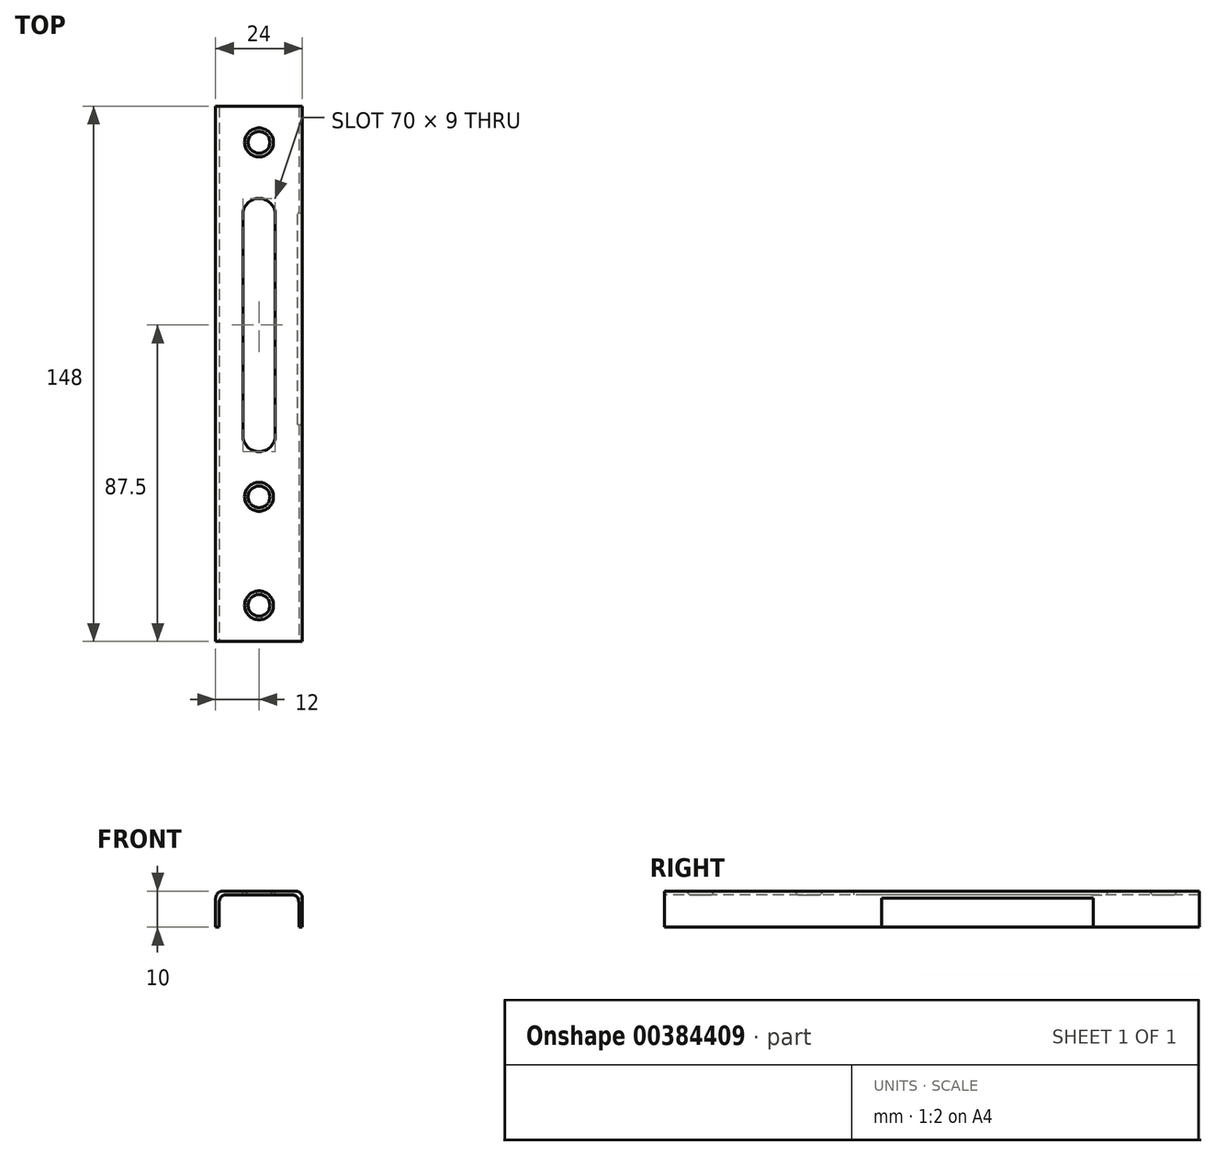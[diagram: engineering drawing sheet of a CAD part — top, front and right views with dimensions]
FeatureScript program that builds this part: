
annotation { "Feature Type Name" : "Feature", "Feature Type Description" : "" }
export const myFeature = defineFeature(function(context is Context, id is Id, definition is map)
    precondition{}
    {
        {
            var Q0;
            Q0=qCreatedBy(makeId("Top.planeOp"),FACE);
            var sketch = newSketch(context, id + "F0", { "sketchPlane" : qUnion([Q0])});
            skLineSegment(sketch, "E0", {"start": v(0, 0) * mm, "end": v(0, 148) * mm});
            skLineSegment(sketch, "E1", {"start": v(0, 148) * mm, "end": v(24, 148) * mm});
            skLineSegment(sketch, "E2", {"start": v(24, 148) * mm, "end": v(24, 0) * mm});
            skLineSegment(sketch, "E3", {"start": v(24, 0) * mm, "end": v(0, 0) * mm});
            skSolve(sketch);
        }
        {
            var Q0;
            Q0 = qSketchRegion(id + "F0", true);
            extrude(context, id + "F1", {"entities" : qUnion([Q0]), "depth" : 10 * mm});
        }
        {
            var Q0;
            Q0=makeQuery(id+"F1.opExtrude","CAP_EDGE",EDGE,{"disambiguationData":[OSD([sQuery(id+"F0.wireOp",EDGE,"E0")])],"isStart":false});
            fillet(context, id + "F2", {"entities" : qUnion([Q0]), "radius" : 2 * mm, "tangentPropagation" : true, "allowEdgeOverflow" : false});
        }
        {
            var Q0;
            Q0=makeQuery(id+"F1.opExtrude","SWEPT_FACE",FACE,{"disambiguationData":[OSD([sQuery(id+"F0.wireOp",EDGE,"E3")])]});
            var sketch = newSketch(context, id + "F3", { "sketchPlane" : qUnion([Q0])});
            skLineSegment(sketch, "E4", {"start": v(1, 0) * mm, "end": v(1, 9) * mm});
            skLineSegment(sketch, "E5", {"start": v(1, 9) * mm, "end": v(23, 9) * mm});
            skLineSegment(sketch, "E6", {"start": v(23, 9) * mm, "end": v(23, 0) * mm});
            skSolve(sketch);
        }
        {
            var Q0;
            Q0 = qSketchRegion(id + "F3", true);
            var Q1;
            {var subQ0=sQuery(id+"F3.wireOp",EDGE,"E4");Q1=makeQuery(id+"F3.imprint","IMPRINT",FACE,{"disambiguationData":[TD([[makeQuery(id+"F3.imprint","IMPRINT",EDGE,{"derivedFrom":subQ0}),-1.0]])]});}
            extrude(context, id + "F4", {"entities" : qUnion([Q0, Q1]), "operationType" : NewBodyOperationType.REMOVE, "endBound" : BoundingType.UP_TO_NEXT, "oppositeDirection" : true, "depth" : 25 * mm});
        }
        {
            var Q0;
            Q0=makeQuery(id+"F4.boolean.opBoolean","COPY",EDGE,{"derivedFrom":makeQuery(id+"F4.opExtrude","SWEPT_EDGE",EDGE,{"disambiguationData":[OSD([sQuery(id+"F3.wireOp",EDGE,"E4"),sQuery(id+"F3.wireOp",EDGE,"E5")])]})});
            fillet(context, id + "F5", {"entities" : qUnion([Q0]), "radius" : 2 * mm, "tangentPropagation" : true, "allowEdgeOverflow" : false});
        }
        {
            var Q0;
            Q0=makeQuery(id+"F1.opExtrude","CAP_FACE",FACE,{"disambiguationData":[OSD([sQuery(id+"F0.wireOp",EDGE,"E0"),sQuery(id+"F0.wireOp",EDGE,"E1"),sQuery(id+"F0.wireOp",EDGE,"E2"),sQuery(id+"F0.wireOp",EDGE,"E3")])],"isStart":false});
            var sketch = newSketch(context, id + "F6", { "sketchPlane" : qUnion([Q0])});
            skLineSegment(sketch, "E7.bottom", {"start": v(16.5, 118) * mm, "end": v(7.5, 118) * mm, "construction": true});
            skLineSegment(sketch, "E7.top", {"start": v(16.5, 57) * mm, "end": v(12, 57) * mm, "construction": true});
            skLineSegment(sketch, "E7.left", {"start": v(16.5, 118) * mm, "end": v(16.5, 57) * mm});
            skLineSegment(sketch, "E7.right", {"start": v(7.5, 118) * mm, "end": v(7.5, 57) * mm});
            skArc(sketch, "E8", {"start": v(16.5, 118) * mm, "mid": v(12, 122.5) * mm, "end": v(7.5, 118) * mm});
            skArc(sketch, "E9", {"start": v(7.5, 57) * mm, "mid": v(12, 52.5) * mm, "end": v(16.5, 57) * mm});
            skSolve(sketch);
        }
        {
            var Q0;
            Q0 = qSketchRegion(id + "F6", true);
            extrude(context, id + "F7", {"entities" : qUnion([Q0]), "operationType" : NewBodyOperationType.REMOVE, "endBound" : BoundingType.UP_TO_NEXT, "oppositeDirection" : true, "depth" : 25 * mm});
        }
        {
            var Q0;
            {var subQ0=sQuery(id+"F0.wireOp",EDGE,"E3");var subQ1=sQuery(id+"F0.wireOp",EDGE,"E2");Q0=makeQuery(id+"F8lvFVKv8dNZHk1_2.boolean.opBoolean","SPLIT",EDGE,{"disambiguationData":[TD([makeQuery(id+"F1.opExtrude","SWEPT_FACE",FACE,{"disambiguationData":[OSD([subQ0])]})])],"derivedFrom":makeQuery(id+"F1.opExtrude","CAP_EDGE",EDGE,{"disambiguationData":[OSD([subQ1])],"isStart":false})});}
            var Q1;
            {var subQ0=sQuery(id+"F0.wireOp",EDGE,"E2");var subQ1=sQuery(id+"F0.wireOp",EDGE,"E1");Q1=makeQuery(id+"F8lvFVKv8dNZHk1_2.boolean.opBoolean","SPLIT",EDGE,{"disambiguationData":[TD([makeQuery(id+"F1.opExtrude","SWEPT_FACE",FACE,{"disambiguationData":[OSD([subQ1])]})])],"derivedFrom":makeQuery(id+"F1.opExtrude","CAP_EDGE",EDGE,{"disambiguationData":[OSD([subQ0])],"isStart":false})});}
            fillet(context, id + "F8", {"entities" : qUnion([Q0, Q1]), "radius" : 2 * mm, "tangentPropagation" : true, "allowEdgeOverflow" : false});
        }
        {
            var Q0;
            {var subQ0=sQuery(id+"F3.wireOp",EDGE,"E5");var subQ1=sQuery(id+"F3.wireOp",EDGE,"E6");Q0=makeQuery(id+"F8lvFVKv8dNZHk1_2.boolean.opBoolean","SPLIT",EDGE,{"disambiguationData":[TD([makeQuery(id+"F1.opExtrude","SWEPT_FACE",FACE,{"disambiguationData":[OSD([sQuery(id+"F0.wireOp",EDGE,"E1")])]})])],"derivedFrom":makeQuery(id+"F4.boolean.opBoolean","COPY",EDGE,{"derivedFrom":makeQuery(id+"F4.opExtrude","SWEPT_EDGE",EDGE,{"disambiguationData":[OSD([subQ0,subQ1])]})})});}
            var Q1;
            {var subQ0=sQuery(id+"F3.wireOp",EDGE,"E5");var subQ1=sQuery(id+"F3.wireOp",EDGE,"E6");Q1=makeQuery(id+"F8lvFVKv8dNZHk1_2.boolean.opBoolean","SPLIT",EDGE,{"disambiguationData":[TD([makeQuery(id+"F1.opExtrude","SWEPT_FACE",FACE,{"disambiguationData":[OSD([sQuery(id+"F0.wireOp",EDGE,"E3")])]})])],"derivedFrom":makeQuery(id+"F4.boolean.opBoolean","COPY",EDGE,{"derivedFrom":makeQuery(id+"F4.opExtrude","SWEPT_EDGE",EDGE,{"disambiguationData":[OSD([subQ0,subQ1])]})})});}
            fillet(context, id + "F9", {"entities" : qUnion([Q0, Q1]), "radius" : 2 * mm, "tangentPropagation" : true, "allowEdgeOverflow" : false});
        }
        {
            var Q0;
            Q0=makeQuery(id+"FK3YLxgNGnwDV2k_1.boolean.opBoolean","MERGE",FACE,{"derivedFrom":[makeQuery(id+"F1.opExtrude","CAP_FACE",FACE,{"disambiguationData":[OSD([sQuery(id+"F0.wireOp",EDGE,"E0"),sQuery(id+"F0.wireOp",EDGE,"E1"),sQuery(id+"F0.wireOp",EDGE,"E2"),sQuery(id+"F0.wireOp",EDGE,"E3")])],"isStart":false}),makeQuery(id+"FK3YLxgNGnwDV2k_1.opExtrude","SWEPT_FACE",FACE,{"disambiguationData":[OSD([sQuery(id+"FW2qu9RNYv4UlEH_1.wireOp",EDGE,"uoAF6b5F-r3LY-Y0Qm-uENl-4oIqOWw2g4q1")])]})]});
            var sketch = newSketch(context, id + "F10", { "sketchPlane" : qUnion([Q0])});
            skPoint(sketch, "E10", {"position": v(12, 138) * mm});
            skPoint(sketch, "E11", {"position": v(12, 40) * mm});
            skPoint(sketch, "E12", {"position": v(12, 10) * mm});
            skSolve(sketch);
        }
        {
            var Q0;
            Q0=sQuery(id+"F10.wireOp",VERTEX,"E10");
            var Q1;
            Q1=sQuery(id+"F10.wireOp",VERTEX,"E11");
            var Q2;
            Q2=sQuery(id+"F10.wireOp",VERTEX,"E12");
            var Q3;
            Q3=makeQuery(id+"F1.opExtrude","SWEPT_BODY",BODY,{"disambiguationData":[OSD([sQuery(id+"F0.wireOp",EDGE,"E0"),sQuery(id+"F0.wireOp",EDGE,"E1"),sQuery(id+"F0.wireOp",EDGE,"E2"),sQuery(id+"F0.wireOp",EDGE,"E3")])]});
            hole(context, id + "F11", {"style" : HoleStyle.C_SINK, "endStyle" : HoleEndStyle.THROUGH, "holeDiameter" : 5 * mm, "cSinkDiameter" : 8 * mm, "cSinkAngle" : 90 * degree, "isTappedThrough" : true, "tappedDepth" : 12 * mm, "tapClearance" : 3, "locations" : qUnion([Q0, Q1, Q2]), "scope" : qUnion([Q3])});
        }
        {
            var Q0;
            Q0=makeQuery(id+"F1.opExtrude","SWEPT_FACE",FACE,{"disambiguationData":[OSD([sQuery(id+"F0.wireOp",EDGE,"E3")])]});
            cPlane(context, id + "F12", {"entities" : qUnion([Q0]), "cplaneType" : CPlaneType.OFFSET, "offset" : 60 * mm, "oppositeDirection" : true, "width" : 150 * mm, "height" : 150 * mm});
        }
        {
            var Q0;
            Q0=makeQuery(id+"F1.opExtrude","SWEPT_FACE",FACE,{"disambiguationData":[OSD([sQuery(id+"F0.wireOp",EDGE,"E2")])]});
            var sketch = newSketch(context, id + "F13", { "sketchPlane" : qUnion([Q0])});
            skLineSegment(sketch, "E13.bottom", {"start": v(60, 0) * mm, "end": v(118.57, 0) * mm});
            skLineSegment(sketch, "E13.top", {"start": v(60, 8) * mm, "end": v(118.57, 8) * mm});
            skLineSegment(sketch, "E13.left", {"start": v(60, 0) * mm, "end": v(60, 8) * mm});
            skLineSegment(sketch, "E13.right", {"start": v(118.57, 0) * mm, "end": v(118.57, 8) * mm});
            skSolve(sketch);
        }
        {
            var Q0;
            Q0=makeQuery(id+"F13.imprint","IMPRINT",FACE,{"disambiguationData":[TD([[makeQuery(id+"F13.imprint","IMPRINT",EDGE,{"derivedFrom":sQuery(id+"F13.wireOp",EDGE,"E13.bottom")}),-1.0]])]});
            extrude(context, id + "F14", {"entities" : qUnion([Q0]), "operationType" : NewBodyOperationType.REMOVE, "endBound" : BoundingType.UP_TO_NEXT, "oppositeDirection" : true, "depth" : 25 * mm});
        }
    });
